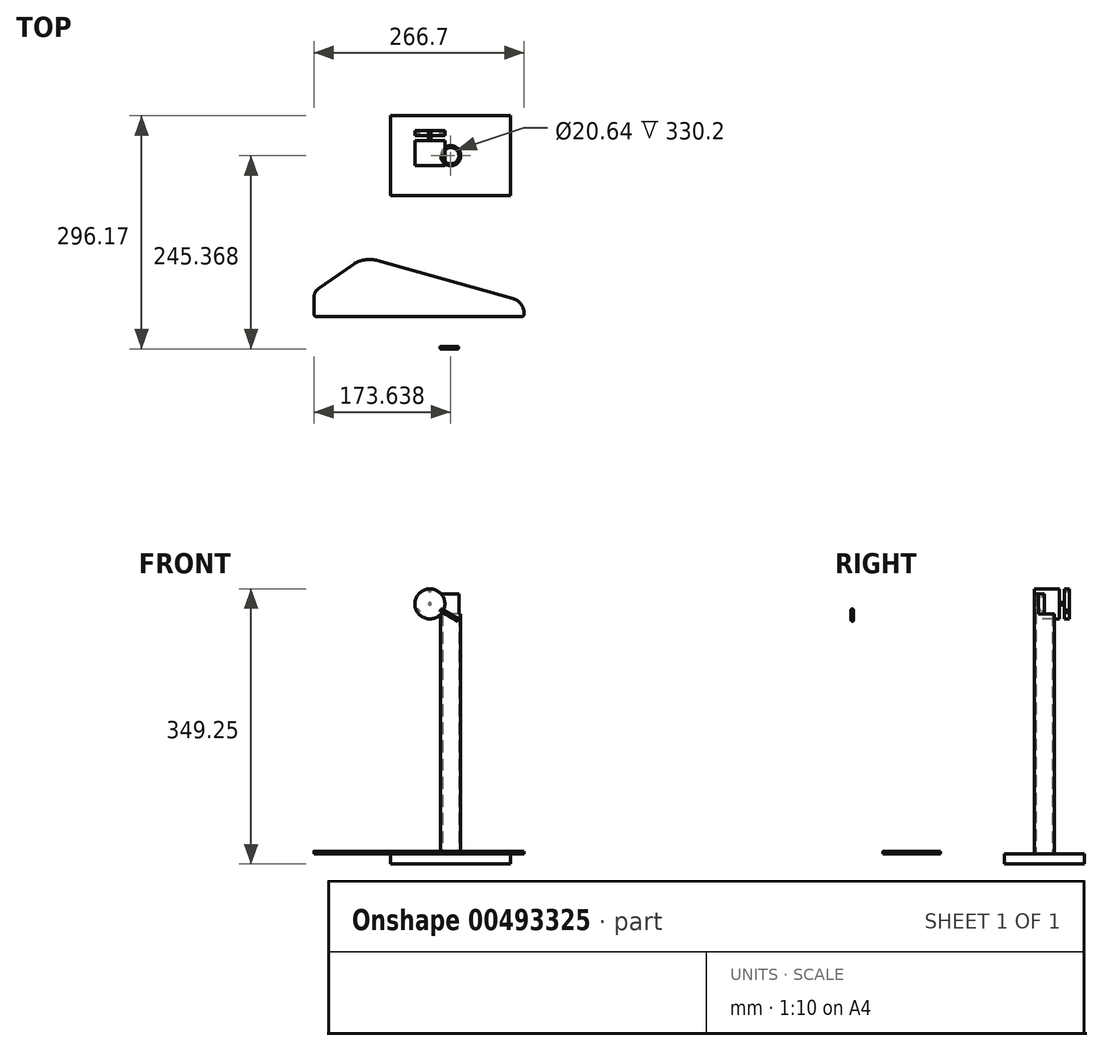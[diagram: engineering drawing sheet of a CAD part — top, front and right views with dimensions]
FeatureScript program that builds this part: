
annotation { "Feature Type Name" : "Feature", "Feature Type Description" : "" }
export const myFeature = defineFeature(function(context is Context, id is Id, definition is map)
    precondition{}
    {
        {
            var Q0;
            Q0=qCreatedBy(makeId("Top.planeOp"),FACE);
            var sketch = newSketch(context, id + "F0", { "sketchPlane" : qUnion([Q0])});
            skLineSegment(sketch, "E0.bottom", {"start": v(-160.38, 7.8) * mm, "end": v(106.32, 7.8) * mm});
            skLineSegment(sketch, "E0.top", {"start": v(-157.2, -68.4) * mm, "end": v(103.15, -68.4) * mm});
            skLineSegment(sketch, "E0.left", {"start": v(-160.38, 7.8) * mm, "end": v(-160.38, -68.4) * mm});
            skLineSegment(sketch, "E0.right", {"start": v(106.32, 7.8) * mm, "end": v(106.32, -68.4) * mm});
            skLineSegment(sketch, "E1", {"start": v(-96.88, 7.8) * mm, "end": v(-96.88, -68.4) * mm, "construction": true});
            skLineSegment(sketch, "E2", {"start": v(-160.38, -65.23) * mm, "end": v(-160.38, -43.26) * mm});
            skLineSegment(sketch, "E3", {"start": v(106.32, -65.23) * mm, "end": v(106.32, -63.78) * mm});
            skLineSegment(sketch, "E4", {"start": v(92.43, -45.44) * mm, "end": v(-79.5, 2.91) * mm});
            skLineSegment(sketch, "E5", {"start": v(-154.96, -32.86) * mm, "end": v(-111.67, -2.55) * mm});
            skPoint(sketch, "E6.visualSharp", {"position": v(106.32, -49.35) * mm});
            skArc(sketch, "E6.filletArc", {"start": v(106.32, -63.78) * mm, "mid": v(102.46, -52.28) * mm, "end": v(92.43, -45.44) * mm});
            skPoint(sketch, "E7.visualSharp", {"position": v(106.32, -68.4) * mm});
            skArc(sketch, "E7.filletArc", {"start": v(103.15, -68.4) * mm, "mid": v(105.4, -67.47) * mm, "end": v(106.32, -65.23) * mm});
            skPoint(sketch, "E8.visualSharp", {"position": v(-96.88, 7.8) * mm});
            skArc(sketch, "E8.filletArc", {"start": v(-79.5, 2.91) * mm, "mid": v(-96.2, 3.8) * mm, "end": v(-111.67, -2.55) * mm});
            skPoint(sketch, "E9.visualSharp", {"position": v(-160.38, -36.65) * mm});
            skArc(sketch, "E9.filletArc", {"start": v(-154.96, -32.86) * mm, "mid": v(-158.94, -37.4) * mm, "end": v(-160.38, -43.26) * mm});
            skPoint(sketch, "E10.visualSharp", {"position": v(-160.38, -68.4) * mm});
            skArc(sketch, "E10.filletArc", {"start": v(-160.38, -65.23) * mm, "mid": v(-159.45, -67.47) * mm, "end": v(-157.2, -68.4) * mm});
            skSolve(sketch);
        }
        {
            var Q0;
            Q0=makeQuery(id+"F0.imprint","IMPRINT",FACE,{"disambiguationData":[TD([[makeQuery(id+"F0.imprint","IMPRINT",EDGE,{"derivedFrom":sQuery(id+"F0.wireOp",EDGE,"E0.top")}),1.0]])]});
            extrude(context, id + "F1", {"entities" : qUnion([Q0]), "depth" : 3.17 * mm});
        }
        {
            var Q0;
            Q0=qCreatedBy(makeId("Top.planeOp"),FACE);
            var sketch = newSketch(context, id + "F2", { "sketchPlane" : qUnion([Q0])});
            skLineSegment(sketch, "E11.bottom", {"start": v(-62.94, 186.98) * mm, "end": v(89.46, 186.98) * mm});
            skLineSegment(sketch, "E11.top", {"start": v(-62.94, 85.38) * mm, "end": v(89.46, 85.38) * mm});
            skLineSegment(sketch, "E11.left", {"start": v(-62.94, 186.98) * mm, "end": v(-62.94, 85.38) * mm});
            skLineSegment(sketch, "E11.right", {"start": v(89.46, 186.98) * mm, "end": v(89.46, 85.38) * mm});
            skCircle(sketch, "E12", {"center": v(13.26, 136.18) * mm, "radius": 12.7 * mm});
            skPoint(sketch, "E12.centerSnap0", {"position": v(-62.94, 136.18) * mm});
            skPoint(sketch, "E12.centerSnap1", {"position": v(13.26, 186.98) * mm});
            skCircle(sketch, "E13", {"center": v(13.26, 136.18) * mm, "radius": 10.32 * mm});
            skSolve(sketch);
        }
        {
            var Q0;
            Q0 = qSketchRegion(id + "F2", true);
            var Q1;
            Q1=makeQuery(id+"F2.imprint","IMPRINT",FACE,{"disambiguationData":[TD([[makeQuery(id+"F2.imprint","IMPRINT",EDGE,{"derivedFrom":sQuery(id+"F2.wireOp",EDGE,"E12")}),1.0]])]});
            var Q2;
            Q2=makeQuery(id+"F2.imprint","IMPRINT",FACE,{"disambiguationData":[TD([[makeQuery(id+"F2.imprint","IMPRINT",EDGE,{"derivedFrom":sQuery(id+"F2.wireOp",EDGE,"E13")}),1.0]])]});
            extrude(context, id + "F3", {"entities" : qUnion([Q0, Q1, Q2]), "oppositeDirection" : true, "depth" : 12.7 * mm});
        }
        {
            var Q0;
            Q0=makeQuery(id+"F2.imprint","IMPRINT",FACE,{"disambiguationData":[TD([[makeQuery(id+"F2.imprint","IMPRINT",EDGE,{"derivedFrom":sQuery(id+"F2.wireOp",EDGE,"E12")}),1.0]])]});
            extrude(context, id + "F4", {"entities" : qUnion([Q0]), "depth" : 304.8 * mm});
        }
        {
            var Q0;
            Q0=makeQuery(id+"F4.opExtrude","CAP_FACE",FACE,{"disambiguationData":[OSD([sQuery(id+"F2.wireOp",EDGE,"E12"),sQuery(id+"F2.wireOp",EDGE,"E13")])],"isStart":false});
            var sketch = newSketch(context, id + "F5", { "sketchPlane" : qUnion([Q0])});
            skCircle(sketch, "E14", {"center": v(13.26, 136.18) * mm, "radius": 12.7 * mm});
            skLineSegment(sketch, "E15", {"start": v(13.26, 136.18) * mm, "end": v(0.56, 136.18) * mm});
            skLineSegment(sketch, "E16", {"start": v(0.56, 136.18) * mm, "end": v(25.96, 136.18) * mm});
            skSolve(sketch);
        }
        {
            var Q0;
            {var subQ0=sQuery(id+"F5.wireOp",EDGE,"E16");var subQ1=sQuery(id+"F5.wireOp",EDGE,"E14");var subQ2=makeQuery(id+"F5.imprint","INTERSECT",VERTEX,{"disambiguationData":[OD(0.0)],"derivedFrom":[subQ1,subQ0]});Q0=makeQuery(id+"F5.imprint","IMPRINT",FACE,{"disambiguationData":[TD([[makeQuery(id+"F5.imprint","IMPRINT",EDGE,{"disambiguationData":[TD([[subQ2,1.0]])],"derivedFrom":subQ1}),1.0]])]});}
            var Q1;
            {var subQ0=sQuery(id+"F5.wireOp",EDGE,"E16");var subQ1=makeQuery(id+"F5.imprint","IMPRINT",VERTEX,{"derivedFrom":subQ0});Q1=makeQuery(id+"F5.imprint","IMPRINT",FACE,{"disambiguationData":[TD([[makeQuery(id+"F5.imprint","IMPRINT",EDGE,{"disambiguationData":[TD([[subQ1,1.0]])],"derivedFrom":subQ0}),1.0]])]});}
            extrude(context, id + "F6", {"entities" : qUnion([Q0, Q1]), "depth" : 25.4 * mm});
        }
        {
            var Q0;
            Q0=makeQuery(id+"F6.opExtrude","SWEPT_FACE",FACE,{"disambiguationData":[OSD([sQuery(id+"F5.wireOp",EDGE,"E16")])]});
            var sketch = newSketch(context, id + "F7", { "sketchPlane" : qUnion([Q0])});
            skCircle(sketch, "E17", {"center": v(13.26, 317.5) * mm, "radius": 12.7 * mm});
            skPoint(sketch, "E17.centerSnap0", {"position": v(0.56, 317.5) * mm});
            skPoint(sketch, "E17.centerSnap1", {"position": v(13.26, 330.2) * mm});
            skCircle(sketch, "E18", {"center": v(13.26, 317.5) * mm, "radius": 14.29 * mm});
            skLineSegment(sketch, "E19", {"start": v(6.71, 304.8) * mm, "end": v(19.8, 304.8) * mm});
            skCircle(sketch, "E20", {"center": v(13.26, 317.5) * mm, "radius": 1.59 * mm});
            skCircle(sketch, "E21", {"center": v(13.26, 317.5) * mm, "radius": 19.05 * mm});
            skSolve(sketch);
        }
        {
            var Q0;
            {var subQ0=sQuery(id+"F7.wireOp",EDGE,"E17");var subQ1=sQuery(id+"F5.wireOp",EDGE,"E16");var subQ2=makeQuery(id+"F6.opExtrude","CAP_EDGE",EDGE,{"disambiguationData":[OSD([subQ1])],"isStart":false});var subQ3=makeQuery(id+"F7.imprint","INTERSECT",VERTEX,{"derivedFrom":[subQ2,subQ0]});Q0=makeQuery(id+"F7.imprint","IMPRINT",FACE,{"disambiguationData":[TD([[makeQuery(id+"F7.imprint","IMPRINT",EDGE,{"disambiguationData":[TD([[subQ3,1.0]])],"derivedFrom":subQ2}),-1.0]])]});}
            var Q1;
            {var subQ0=sQuery(id+"F7.wireOp",EDGE,"E18");var subQ1=makeQuery(id+"F6.opExtrude","CAP_EDGE",EDGE,{"disambiguationData":[OSD([sQuery(id+"F5.wireOp",EDGE,"E16")])],"isStart":false});var subQ2=makeQuery(id+"F7.imprint","INTERSECT",VERTEX,{"disambiguationData":[OD(0.0)],"derivedFrom":[subQ1,subQ0]});Q1=makeQuery(id+"F7.imprint","IMPRINT",FACE,{"disambiguationData":[TD([[makeQuery(id+"F7.imprint","IMPRINT",EDGE,{"disambiguationData":[TD([[subQ2,-1.0]])],"derivedFrom":subQ0}),1.0]])]});}
            var Q2;
            {var subQ0=sQuery(id+"F7.wireOp",EDGE,"E17");var subQ1=sQuery(id+"F5.wireOp",EDGE,"E16");var subQ2=makeQuery(id+"F6.opExtrude","CAP_EDGE",EDGE,{"disambiguationData":[OSD([subQ1])],"isStart":false});var subQ3=makeQuery(id+"F7.imprint","INTERSECT",VERTEX,{"derivedFrom":[subQ2,subQ0]});Q2=makeQuery(id+"F7.imprint","IMPRINT",FACE,{"disambiguationData":[TD([[makeQuery(id+"F7.imprint","IMPRINT",EDGE,{"disambiguationData":[TD([[subQ3,-1.0]])],"derivedFrom":subQ2}),-1.0]])]});}
            var Q3;
            {var subQ0=sQuery(id+"F7.wireOp",EDGE,"E18");var subQ1=sQuery(id+"F5.wireOp",EDGE,"E16");var subQ2=sQuery(id+"F5.wireOp",EDGE,"E14");var subQ3=makeQuery(id+"F6.opExtrude","SWEPT_EDGE",EDGE,{"disambiguationData":[OSD([subQ2,subQ1]),TDD([makeQuery(id+"F5.imprint","INTERSECT",VERTEX,{"disambiguationData":[OD(1.0)],"derivedFrom":[subQ2,subQ1]})])]});var subQ4=makeQuery(id+"F7.imprint","INTERSECT",VERTEX,{"disambiguationData":[OD(0.0)],"derivedFrom":[subQ3,subQ0]});Q3=makeQuery(id+"F7.imprint","IMPRINT",FACE,{"disambiguationData":[TD([[makeQuery(id+"F7.imprint","IMPRINT",EDGE,{"disambiguationData":[TD([[subQ4,1.0]])],"derivedFrom":subQ0}),1.0]])]});}
            var Q4;
            {var subQ0=sQuery(id+"F7.wireOp",EDGE,"E18");var subQ1=sQuery(id+"F5.wireOp",EDGE,"E16");var subQ2=makeQuery(id+"F6.opExtrude","CAP_EDGE",EDGE,{"disambiguationData":[OSD([subQ1])],"isStart":true});var subQ3=makeQuery(id+"F7.imprint","INTERSECT",VERTEX,{"disambiguationData":[OD(1.0)],"derivedFrom":[subQ2,subQ0,sQuery(id+"F7.wireOp",EDGE,"E19")]});Q4=makeQuery(id+"F7.imprint","IMPRINT",FACE,{"disambiguationData":[TD([[makeQuery(id+"F7.imprint","IMPRINT",EDGE,{"disambiguationData":[TD([[subQ3,-1.0]])],"derivedFrom":subQ0}),-1.0]])]});}
            var Q5;
            {var subQ0=sQuery(id+"F7.wireOp",EDGE,"E19");var subQ1=sQuery(id+"F7.wireOp",EDGE,"E17");var subQ2=makeQuery(id+"F7.imprint","INTERSECT",VERTEX,{"derivedFrom":[subQ1,subQ0]});Q5=makeQuery(id+"F7.imprint","IMPRINT",FACE,{"disambiguationData":[TD([[makeQuery(id+"F7.imprint","IMPRINT",EDGE,{"disambiguationData":[TD([[subQ2,-1.0]])],"derivedFrom":subQ0}),1.0]])]});}
            var Q6;
            {var subQ0=sQuery(id+"F7.wireOp",EDGE,"E19");var subQ1=sQuery(id+"F7.wireOp",EDGE,"E17");var subQ2=makeQuery(id+"F7.imprint","INTERSECT",VERTEX,{"derivedFrom":[subQ1,subQ0]});Q6=makeQuery(id+"F7.imprint","IMPRINT",FACE,{"disambiguationData":[TD([[makeQuery(id+"F7.imprint","IMPRINT",EDGE,{"disambiguationData":[TD([[subQ2,1.0]])],"derivedFrom":subQ0}),1.0]])]});}
            var Q7;
            {var subQ0=sQuery(id+"F7.wireOp",EDGE,"E18");var subQ1=sQuery(id+"F5.wireOp",EDGE,"E16");var subQ2=sQuery(id+"F5.wireOp",EDGE,"E14");var subQ3=makeQuery(id+"F6.opExtrude","SWEPT_EDGE",EDGE,{"disambiguationData":[OSD([subQ2,subQ1]),TDD([makeQuery(id+"F5.imprint","INTERSECT",VERTEX,{"disambiguationData":[OD(0.0)],"derivedFrom":[subQ2,subQ1]})])]});var subQ4=makeQuery(id+"F7.imprint","INTERSECT",VERTEX,{"disambiguationData":[OD(0.0)],"derivedFrom":[subQ3,subQ0]});Q7=makeQuery(id+"F7.imprint","IMPRINT",FACE,{"disambiguationData":[TD([[makeQuery(id+"F7.imprint","IMPRINT",EDGE,{"disambiguationData":[TD([[subQ4,-1.0]])],"derivedFrom":subQ0}),1.0]])]});}
            var Q8;
            Q8=makeQuery(id+"F7.imprint","IMPRINT",FACE,{"disambiguationData":[TD([[makeQuery(id+"F7.imprint","IMPRINT",EDGE,{"derivedFrom":sQuery(id+"F7.wireOp",EDGE,"E20")}),-1.0]])]});
            var Q9;
            Q9=makeQuery(id+"F7.imprint","IMPRINT",FACE,{"disambiguationData":[TD([[makeQuery(id+"F7.imprint","IMPRINT",EDGE,{"derivedFrom":sQuery(id+"F7.wireOp",EDGE,"E20")}),1.0]])]});
            var Q10;
            {var subQ0=sQuery(id+"F7.wireOp",EDGE,"E18");var subQ1=sQuery(id+"F5.wireOp",EDGE,"E16");var subQ2=makeQuery(id+"F6.opExtrude","CAP_EDGE",EDGE,{"disambiguationData":[OSD([subQ1])],"isStart":true});var subQ3=makeQuery(id+"F7.imprint","INTERSECT",VERTEX,{"disambiguationData":[OD(0.0)],"derivedFrom":[subQ2,subQ0,sQuery(id+"F7.wireOp",EDGE,"E19")]});Q10=makeQuery(id+"F7.imprint","IMPRINT",FACE,{"disambiguationData":[TD([[makeQuery(id+"F7.imprint","IMPRINT",EDGE,{"disambiguationData":[TD([[subQ3,1.0]])],"derivedFrom":subQ0}),-1.0]])]});}
            extrude(context, id + "F8", {"entities" : qUnion([Q0, Q1, Q2, Q3, Q4, Q5, Q6, Q7, Q8, Q9, Q10]), "operationType" : NewBodyOperationType.ADD, "depth" : 19.05 * mm, "hasSecondDirection" : true, "secondDirectionOppositeDirection" : true, "secondDirectionDepth" : 12.7 * mm});
        }
        {
            var Q0;
            Q0=makeQuery(id+"F8.boolean.opBoolean","SPLIT",FACE,{"disambiguationData":[OD(1.0)],"derivedFrom":makeQuery(id+"F6.opExtrude","SWEPT_FACE",FACE,{"disambiguationData":[OSD([sQuery(id+"F5.wireOp",EDGE,"E16")])]})});
            var Q1;
            Q1=makeQuery(id+"F8.boolean.opBoolean","SPLIT",FACE,{"disambiguationData":[OD(0.0)],"derivedFrom":makeQuery(id+"F6.opExtrude","SWEPT_FACE",FACE,{"disambiguationData":[OSD([sQuery(id+"F5.wireOp",EDGE,"E16")])]})});
            extrude(context, id + "F9", {"entities" : qUnion([Q0, Q1]), "operationType" : NewBodyOperationType.REMOVE, "oppositeDirection" : true, "depth" : 25.4 * mm});
        }
        {
            var Q0;
            Q0=makeQuery(id+"F7.imprint","IMPRINT",FACE,{"disambiguationData":[TD([[makeQuery(id+"F7.imprint","IMPRINT",EDGE,{"derivedFrom":sQuery(id+"F7.wireOp",EDGE,"E20")}),1.0]])]});
            extrude(context, id + "F10", {"entities" : qUnion([Q0]), "operationType" : NewBodyOperationType.ADD, "depth" : 25.4 * mm});
        }
        {
            var Q0;
            Q0=makeQuery(id+"F7.imprint","IMPRINT",FACE,{"disambiguationData":[TD([[makeQuery(id+"F7.imprint","IMPRINT",EDGE,{"derivedFrom":sQuery(id+"F7.wireOp",EDGE,"E20")}),-1.0]])]});
            var Q1;
            {var subQ0=sQuery(id+"F7.wireOp",EDGE,"E19");var subQ1=sQuery(id+"F7.wireOp",EDGE,"E17");var subQ2=makeQuery(id+"F7.imprint","INTERSECT",VERTEX,{"derivedFrom":[subQ1,subQ0]});Q1=makeQuery(id+"F7.imprint","IMPRINT",FACE,{"disambiguationData":[TD([[makeQuery(id+"F7.imprint","IMPRINT",EDGE,{"disambiguationData":[TD([[subQ2,1.0]])],"derivedFrom":subQ0}),1.0]])]});}
            var Q2;
            Q2=makeQuery(id+"F7.imprint","IMPRINT",FACE,{"disambiguationData":[TD([[makeQuery(id+"F7.imprint","IMPRINT",EDGE,{"derivedFrom":sQuery(id+"F7.wireOp",EDGE,"E21")}),1.0]])]});
            var Q3;
            {var subQ0=sQuery(id+"F7.wireOp",EDGE,"E19");var subQ1=sQuery(id+"F7.wireOp",EDGE,"E17");var subQ2=makeQuery(id+"F7.imprint","INTERSECT",VERTEX,{"derivedFrom":[subQ1,subQ0]});Q3=makeQuery(id+"F7.imprint","IMPRINT",FACE,{"disambiguationData":[TD([[makeQuery(id+"F7.imprint","IMPRINT",EDGE,{"disambiguationData":[TD([[subQ2,-1.0]])],"derivedFrom":subQ0}),1.0]])]});}
            var Q4;
            {var subQ0=sQuery(id+"F7.wireOp",EDGE,"E17");var subQ1=sQuery(id+"F5.wireOp",EDGE,"E16");var subQ2=makeQuery(id+"F6.opExtrude","CAP_EDGE",EDGE,{"disambiguationData":[OSD([subQ1])],"isStart":false});var subQ3=makeQuery(id+"F7.imprint","INTERSECT",VERTEX,{"derivedFrom":[subQ2,subQ0]});Q4=makeQuery(id+"F7.imprint","IMPRINT",FACE,{"disambiguationData":[TD([[makeQuery(id+"F7.imprint","IMPRINT",EDGE,{"disambiguationData":[TD([[subQ3,1.0]])],"derivedFrom":subQ2}),-1.0]])]});}
            var Q5;
            {var subQ0=sQuery(id+"F7.wireOp",EDGE,"E18");var subQ1=sQuery(id+"F5.wireOp",EDGE,"E16");var subQ2=makeQuery(id+"F6.opExtrude","CAP_EDGE",EDGE,{"disambiguationData":[OSD([subQ1])],"isStart":false});var subQ3=makeQuery(id+"F7.imprint","INTERSECT",VERTEX,{"disambiguationData":[OD(0.0)],"derivedFrom":[subQ2,subQ0]});Q5=makeQuery(id+"F7.imprint","IMPRINT",FACE,{"disambiguationData":[TD([[makeQuery(id+"F7.imprint","IMPRINT",EDGE,{"disambiguationData":[TD([[subQ3,1.0]])],"derivedFrom":subQ0}),-1.0]])]});}
            var Q6;
            {var subQ0=sQuery(id+"F7.wireOp",EDGE,"E18");var subQ1=sQuery(id+"F5.wireOp",EDGE,"E16");var subQ2=makeQuery(id+"F6.opExtrude","CAP_EDGE",EDGE,{"disambiguationData":[OSD([subQ1])],"isStart":false});var subQ3=makeQuery(id+"F7.imprint","INTERSECT",VERTEX,{"disambiguationData":[OD(1.0)],"derivedFrom":[subQ2,subQ0]});Q6=makeQuery(id+"F7.imprint","IMPRINT",FACE,{"disambiguationData":[TD([[makeQuery(id+"F7.imprint","IMPRINT",EDGE,{"disambiguationData":[TD([[subQ3,-1.0]])],"derivedFrom":subQ0}),-1.0]])]});}
            var Q7;
            {var subQ0=sQuery(id+"F7.wireOp",EDGE,"E18");var subQ1=sQuery(id+"F5.wireOp",EDGE,"E16");var subQ2=makeQuery(id+"F6.opExtrude","CAP_EDGE",EDGE,{"disambiguationData":[OSD([subQ1])],"isStart":true});var subQ3=makeQuery(id+"F7.imprint","INTERSECT",VERTEX,{"disambiguationData":[OD(0.0)],"derivedFrom":[subQ2,subQ0,sQuery(id+"F7.wireOp",EDGE,"E19")]});Q7=makeQuery(id+"F7.imprint","IMPRINT",FACE,{"disambiguationData":[TD([[makeQuery(id+"F7.imprint","IMPRINT",EDGE,{"disambiguationData":[TD([[subQ3,1.0]])],"derivedFrom":subQ0}),-1.0]])]});}
            var Q8;
            {var subQ0=sQuery(id+"F7.wireOp",EDGE,"E17");var subQ1=sQuery(id+"F5.wireOp",EDGE,"E16");var subQ2=makeQuery(id+"F6.opExtrude","CAP_EDGE",EDGE,{"disambiguationData":[OSD([subQ1])],"isStart":false});var subQ3=makeQuery(id+"F7.imprint","INTERSECT",VERTEX,{"derivedFrom":[subQ2,subQ0]});Q8=makeQuery(id+"F7.imprint","IMPRINT",FACE,{"disambiguationData":[TD([[makeQuery(id+"F7.imprint","IMPRINT",EDGE,{"disambiguationData":[TD([[subQ3,-1.0]])],"derivedFrom":subQ2}),-1.0]])]});}
            var Q9;
            {var subQ0=sQuery(id+"F7.wireOp",EDGE,"E18");var subQ1=sQuery(id+"F5.wireOp",EDGE,"E16");var subQ2=sQuery(id+"F5.wireOp",EDGE,"E14");var subQ3=makeQuery(id+"F6.opExtrude","SWEPT_EDGE",EDGE,{"disambiguationData":[OSD([subQ2,subQ1]),TDD([makeQuery(id+"F5.imprint","INTERSECT",VERTEX,{"disambiguationData":[OD(0.0)],"derivedFrom":[subQ2,subQ1]})])]});var subQ4=makeQuery(id+"F7.imprint","INTERSECT",VERTEX,{"disambiguationData":[OD(0.0)],"derivedFrom":[subQ3,subQ0]});Q9=makeQuery(id+"F7.imprint","IMPRINT",FACE,{"disambiguationData":[TD([[makeQuery(id+"F7.imprint","IMPRINT",EDGE,{"disambiguationData":[TD([[subQ4,-1.0]])],"derivedFrom":subQ0}),1.0]])]});}
            var Q10;
            {var subQ0=sQuery(id+"F7.wireOp",EDGE,"E18");var subQ1=makeQuery(id+"F6.opExtrude","CAP_EDGE",EDGE,{"disambiguationData":[OSD([sQuery(id+"F5.wireOp",EDGE,"E16")])],"isStart":false});var subQ2=makeQuery(id+"F7.imprint","INTERSECT",VERTEX,{"disambiguationData":[OD(0.0)],"derivedFrom":[subQ1,subQ0]});Q10=makeQuery(id+"F7.imprint","IMPRINT",FACE,{"disambiguationData":[TD([[makeQuery(id+"F7.imprint","IMPRINT",EDGE,{"disambiguationData":[TD([[subQ2,-1.0]])],"derivedFrom":subQ0}),1.0]])]});}
            var Q11;
            {var subQ0=sQuery(id+"F7.wireOp",EDGE,"E18");var subQ1=sQuery(id+"F5.wireOp",EDGE,"E16");var subQ2=makeQuery(id+"F6.opExtrude","CAP_EDGE",EDGE,{"disambiguationData":[OSD([subQ1])],"isStart":true});var subQ3=makeQuery(id+"F7.imprint","INTERSECT",VERTEX,{"disambiguationData":[OD(1.0)],"derivedFrom":[subQ2,subQ0,sQuery(id+"F7.wireOp",EDGE,"E19")]});Q11=makeQuery(id+"F7.imprint","IMPRINT",FACE,{"disambiguationData":[TD([[makeQuery(id+"F7.imprint","IMPRINT",EDGE,{"disambiguationData":[TD([[subQ3,-1.0]])],"derivedFrom":subQ0}),-1.0]])]});}
            var Q12;
            {var subQ0=sQuery(id+"F7.wireOp",EDGE,"E19");var subQ5=makeQuery(id+"F7.imprint","INTERSECT",VERTEX,{"derivedFrom":[sQuery(id+"F7.wireOp",EDGE,"E17"),subQ0]});Q12=makeQuery(id+"F7.imprint","IMPRINT",FACE,{"disambiguationData":[TD([[makeQuery(id+"F7.imprint","IMPRINT",EDGE,{"disambiguationData":[TD([[subQ5,1.0]])],"derivedFrom":subQ0}),-1.0]])]});}
            var Q13;
            Q13=makeQuery(id+"F7.imprint","IMPRINT",FACE,{"disambiguationData":[TD([[makeQuery(id+"F7.imprint","IMPRINT",EDGE,{"derivedFrom":sQuery(id+"F7.wireOp",EDGE,"E20")}),1.0]])]});
            var Q14;
            {var subQ0=sQuery(id+"F7.wireOp",EDGE,"E18");var subQ1=sQuery(id+"F5.wireOp",EDGE,"E16");var subQ2=sQuery(id+"F5.wireOp",EDGE,"E14");var subQ3=makeQuery(id+"F6.opExtrude","SWEPT_EDGE",EDGE,{"disambiguationData":[OSD([subQ2,subQ1]),TDD([makeQuery(id+"F5.imprint","INTERSECT",VERTEX,{"disambiguationData":[OD(1.0)],"derivedFrom":[subQ2,subQ1]})])]});var subQ4=makeQuery(id+"F7.imprint","INTERSECT",VERTEX,{"disambiguationData":[OD(0.0)],"derivedFrom":[subQ3,subQ0]});Q14=makeQuery(id+"F7.imprint","IMPRINT",FACE,{"disambiguationData":[TD([[makeQuery(id+"F7.imprint","IMPRINT",EDGE,{"disambiguationData":[TD([[subQ4,1.0]])],"derivedFrom":subQ0}),1.0]])]});}
            extrude(context, id + "F11", {"entities" : qUnion([Q0, Q1, Q2, Q3, Q4, Q5, Q6, Q7, Q8, Q9, Q10, Q11, Q12, Q13, Q14]), "operationType" : NewBodyOperationType.ADD, "depth" : 31.75 * mm, "hasSecondDirection" : true, "secondDirectionOppositeDirection" : false, "secondDirectionDepth" : 25.4 * mm});
        }
        {
            var Q0;
            Q0=makeQuery(id+"F11.opExtrude","CAP_FACE",FACE,{"disambiguationData":[OSD([sQuery(id+"F7.wireOp",EDGE,"E21")])],"isStart":false});
            var sketch = newSketch(context, id + "F12", { "sketchPlane" : qUnion([Q0])});
            skCircle(sketch, "E22", {"center": v(13.26, 317.5) * mm, "radius": 19.05 * mm});
            skLineSegment(sketch, "E23", {"start": v(13.26, 317.5) * mm, "end": v(13.26, 336.55) * mm, "construction": true});
            skLineSegment(sketch, "E24", {"start": v(13.26, 333.32) * mm, "end": v(11.67, 333.32) * mm});
            skLineSegment(sketch, "E25", {"start": v(11.67, 333.32) * mm, "end": v(11.67, 336.48) * mm});
            skLineSegment(sketch, "E26", {"start": v(13.26, 333.32) * mm, "end": v(14.85, 333.32) * mm});
            skLineSegment(sketch, "E27", {"start": v(14.85, 333.32) * mm, "end": v(14.85, 336.48) * mm});
            skLineSegment(sketch, "E28.1.0", {"start": v(-1.24, 310.96) * mm, "end": v(-3.98, 309.38) * mm});
            skLineSegment(sketch, "E28.1.1", {"start": v(-0.44, 309.59) * mm, "end": v(-1.24, 310.96) * mm});
            skLineSegment(sketch, "E28.1.2", {"start": v(0.35, 308.21) * mm, "end": v(-2.39, 306.63) * mm});
            skLineSegment(sketch, "E28.1.3", {"start": v(-0.44, 309.59) * mm, "end": v(0.35, 308.21) * mm});
            skLineSegment(sketch, "E28.2.0", {"start": v(26.17, 308.21) * mm, "end": v(28.9, 306.63) * mm});
            skLineSegment(sketch, "E28.2.1", {"start": v(26.96, 309.59) * mm, "end": v(26.17, 308.21) * mm});
            skLineSegment(sketch, "E28.2.2", {"start": v(27.75, 310.96) * mm, "end": v(30.5, 309.38) * mm});
            skLineSegment(sketch, "E28.2.3", {"start": v(26.96, 309.59) * mm, "end": v(27.75, 310.96) * mm});
            skSolve(sketch);
        }
        {
            var Q0;
            {var subQ1=sQuery(id+"F12.wireOp",EDGE,"E28.2.0");Q0=makeQuery(id+"F12.imprint","IMPRINT",FACE,{"disambiguationData":[TD([[makeQuery(id+"F12.imprint","IMPRINT",EDGE,{"derivedFrom":subQ1}),1.0]])]});}
            var Q1;
            Q1=makeQuery(id+"F12.imprint","IMPRINT",FACE,{"disambiguationData":[TD([[makeQuery(id+"F12.imprint","IMPRINT",EDGE,{"derivedFrom":sQuery(id+"F12.wireOp",EDGE,"E24")}),-1.0]])]});
            var Q2;
            {var subQ0=sQuery(id+"F12.wireOp",EDGE,"E28.1.0");Q2=makeQuery(id+"F12.imprint","IMPRINT",FACE,{"disambiguationData":[TD([[makeQuery(id+"F12.imprint","IMPRINT",EDGE,{"derivedFrom":subQ0}),1.0]])]});}
            extrude(context, id + "F13", {"entities" : qUnion([Q0, Q1, Q2]), "operationType" : NewBodyOperationType.REMOVE, "oppositeDirection" : true, "depth" : 9.9 * mm});
        }
        {
            var Q0;
            Q0=makeQuery(id+"F13.boolean.opBoolean","COPY",FACE,{"derivedFrom":makeQuery(id+"F13.opExtrude","SWEPT_FACE",FACE,{"disambiguationData":[OSD([sQuery(id+"F12.wireOp",EDGE,"E28.1.1"),sQuery(id+"F12.wireOp",EDGE,"E28.1.3")])]})});
            var sketch = newSketch(context, id + "F14", { "sketchPlane" : qUnion([Q0])});
            skCircle(sketch, "E29", {"center": v(-107.6, 268.33) * mm, "radius": 1.59 * mm});
            skPoint(sketch, "E29.centerSnap0", {"position": v(-107.6, 269.92) * mm});
            skPoint(sketch, "E29.centerSnap1", {"position": v(-110.78, 268.33) * mm});
            skSolve(sketch);
        }
        {
            var Q0;
            {var subQ0=sQuery(id+"F14.wireOp",EDGE,"E29");var subQ1=makeQuery(id+"F14.imprint","INTERSECT",VERTEX,{"derivedFrom":[makeQuery(id+"F13.boolean.opBoolean","COPY",EDGE,{"derivedFrom":makeQuery(id+"F13.opExtrude","SWEPT_EDGE",EDGE,{"disambiguationData":[OSD([sQuery(id+"F12.wireOp",EDGE,"E28.1.0"),sQuery(id+"F12.wireOp",EDGE,"E28.1.1")])]})}),subQ0]});Q0=makeQuery(id+"F14.imprint","IMPRINT",FACE,{"disambiguationData":[TD([[makeQuery(id+"F14.imprint","IMPRINT",EDGE,{"disambiguationData":[TD([[subQ1,-1.0]])],"derivedFrom":subQ0}),1.0]])]});}
            extrude(context, id + "F15", {"entities" : qUnion([Q0]), "depth" : 25.4 * mm});
        }
    });
